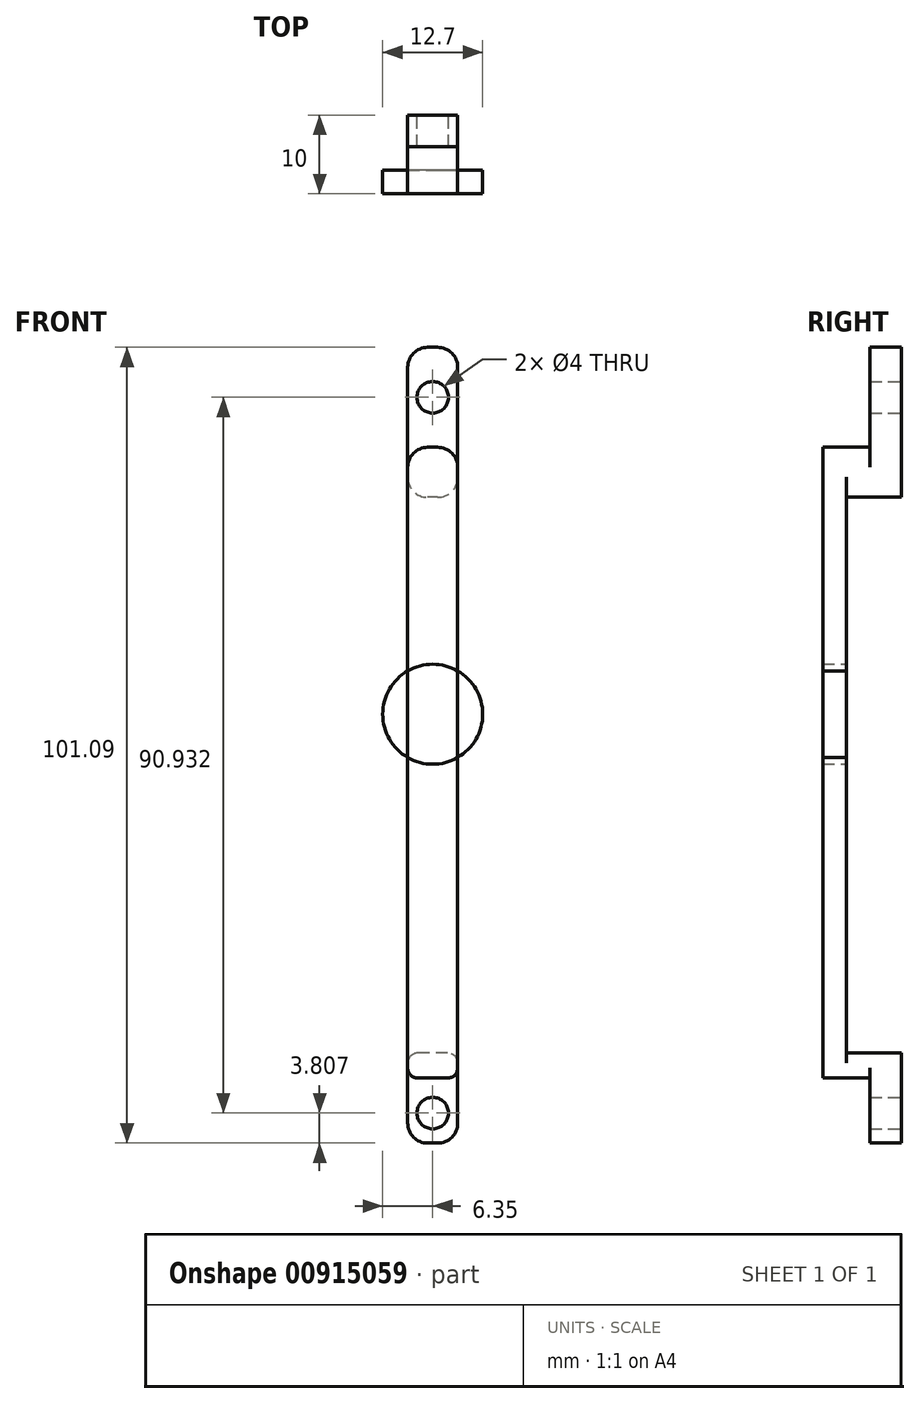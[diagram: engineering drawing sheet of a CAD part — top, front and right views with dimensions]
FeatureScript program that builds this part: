
annotation { "Feature Type Name" : "Feature", "Feature Type Description" : "" }
export const myFeature = defineFeature(function(context is Context, id is Id, definition is map)
    precondition{}
    {
        {
            var Q0;
            Q0=qCreatedBy(makeId("Front.planeOp"),FACE);
            var sketch = newSketch(context, id + "F0", { "sketchPlane" : qUnion([Q0])});
            skCircle(sketch, "E0", {"center": v(0, 0) * mm, "radius": 6.35 * mm});
            skLineSegment(sketch, "E1", {"start": v(0, 0) * mm, "end": v(0, 16.95) * mm, "construction": true});
            skLineSegment(sketch, "E2", {"start": v(0, 0) * mm, "end": v(0, -23.11) * mm, "construction": true});
            skLineSegment(sketch, "E3.bottom", {"start": v(-3.17, 0) * mm, "end": v(3.18, 0) * mm});
            skLineSegment(sketch, "E3.top", {"start": v(-3.17, 33.9) * mm, "end": v(3.18, 33.9) * mm});
            skLineSegment(sketch, "E3.left", {"start": v(-3.17, 0) * mm, "end": v(-3.17, 33.9) * mm});
            skLineSegment(sketch, "E3.right", {"start": v(3.18, 0) * mm, "end": v(3.18, 33.9) * mm});
            skPoint(sketch, "E3.middle", {"position": v(0, 16.95) * mm});
            skLineSegment(sketch, "E4.bottom", {"start": v(3.18, 0) * mm, "end": v(-3.17, 0) * mm});
            skLineSegment(sketch, "E4.top", {"start": v(3.18, -46.23) * mm, "end": v(-3.17, -46.23) * mm});
            skLineSegment(sketch, "E4.left", {"start": v(3.18, 0) * mm, "end": v(3.18, -46.23) * mm});
            skLineSegment(sketch, "E4.right", {"start": v(-3.17, 0) * mm, "end": v(-3.17, -46.23) * mm});
            skPoint(sketch, "E4.middle", {"position": v(0, -23.11) * mm});
            skSolve(sketch);
        }
        {
            var Q0;
            {var subQ5=sQuery(id+"F0.wireOp",EDGE,"E3.top");Q0=makeQuery(id+"F0.imprint","IMPRINT",FACE,{"disambiguationData":[TD([[makeQuery(id+"F0.imprint","IMPRINT",EDGE,{"derivedFrom":subQ5}),-1.0]])]});}
            var Q1;
            {var subQ0=sQuery(id+"F0.wireOp",EDGE,"E3.left");var subQ1=sQuery(id+"F0.wireOp",EDGE,"E0");var subQ2=makeQuery(id+"F0.imprint","INTERSECT",VERTEX,{"derivedFrom":[subQ1,subQ0]});Q1=makeQuery(id+"F0.imprint","IMPRINT",FACE,{"disambiguationData":[TD([[makeQuery(id+"F0.imprint","IMPRINT",EDGE,{"disambiguationData":[TD([[subQ2,-1.0]])],"derivedFrom":subQ1}),1.0]])]});}
            var Q2;
            {var subQ5=sQuery(id+"F0.wireOp",EDGE,"E4.bottom");Q2=makeQuery(id+"F0.imprint","IMPRINT",FACE,{"disambiguationData":[TD([[makeQuery(id+"F0.imprint","IMPRINT",EDGE,{"derivedFrom":subQ5}),-1.0]])]});}
            var Q3;
            {var subQ0=sQuery(id+"F0.wireOp",EDGE,"E3.right");var subQ1=sQuery(id+"F0.wireOp",EDGE,"E0");var subQ2=makeQuery(id+"F0.imprint","INTERSECT",VERTEX,{"derivedFrom":[subQ1,subQ0]});Q3=makeQuery(id+"F0.imprint","IMPRINT",FACE,{"disambiguationData":[TD([[makeQuery(id+"F0.imprint","IMPRINT",EDGE,{"disambiguationData":[TD([[subQ2,1.0]])],"derivedFrom":subQ1}),1.0]])]});}
            var Q4;
            {var subQ5=sQuery(id+"F0.wireOp",EDGE,"E4.bottom");Q4=makeQuery(id+"F0.imprint","IMPRINT",FACE,{"disambiguationData":[TD([[makeQuery(id+"F0.imprint","IMPRINT",EDGE,{"derivedFrom":subQ5}),1.0]])]});}
            var Q5;
            {var subQ5=sQuery(id+"F0.wireOp",EDGE,"E4.top");Q5=makeQuery(id+"F0.imprint","IMPRINT",FACE,{"disambiguationData":[TD([[makeQuery(id+"F0.imprint","IMPRINT",EDGE,{"derivedFrom":subQ5}),-1.0]])]});}
            extrude(context, id + "F1", {"entities" : qUnion([Q0, Q1, Q2, Q3, Q4, Q5]), "depth" : 3 * mm, "offsetDistance" : 25.4 * mm});
        }
        {
            var Q0;
            Q0=makeQuery(id+"F1.opExtrude","CAP_FACE",FACE,{"disambiguationData":[OSD([sQuery(id+"F0.wireOp",EDGE,"E0"),sQuery(id+"F0.wireOp",EDGE,"E3.top"),sQuery(id+"F0.wireOp",EDGE,"E3.left"),sQuery(id+"F0.wireOp",EDGE,"E3.right"),sQuery(id+"F0.wireOp",EDGE,"E4.top"),sQuery(id+"F0.wireOp",EDGE,"E4.left"),sQuery(id+"F0.wireOp",EDGE,"E4.right")])],"isStart":true});
            var sketch = newSketch(context, id + "F2", { "sketchPlane" : qUnion([Q0])});
            skLineSegment(sketch, "E5.bottom", {"start": v(-3.18, 33.9) * mm, "end": v(3.17, 33.9) * mm});
            skLineSegment(sketch, "E5.top", {"start": v(-3.18, 27.56) * mm, "end": v(3.17, 27.56) * mm});
            skLineSegment(sketch, "E5.left", {"start": v(-3.18, 33.9) * mm, "end": v(-3.18, 27.56) * mm});
            skLineSegment(sketch, "E5.right", {"start": v(3.17, 33.9) * mm, "end": v(3.17, 27.56) * mm});
            skLineSegment(sketch, "E6.bottom", {"start": v(-3.18, -46.23) * mm, "end": v(3.17, -46.23) * mm});
            skLineSegment(sketch, "E6.top", {"start": v(-3.18, -43.05) * mm, "end": v(3.17, -43.05) * mm});
            skLineSegment(sketch, "E6.left", {"start": v(-3.18, -46.23) * mm, "end": v(-3.18, -43.05) * mm});
            skLineSegment(sketch, "E6.right", {"start": v(3.17, -46.23) * mm, "end": v(3.17, -43.05) * mm});
            skSolve(sketch);
        }
        {
            var Q0;
            Q0=makeQuery(id+"F2.imprint","IMPRINT",FACE,{"disambiguationData":[TD([[makeQuery(id+"F2.imprint","IMPRINT",EDGE,{"derivedFrom":sQuery(id+"F2.wireOp",EDGE,"E5.bottom")}),1.0]])]});
            var Q1;
            Q1=makeQuery(id+"F2.imprint","IMPRINT",FACE,{"disambiguationData":[TD([[makeQuery(id+"F2.imprint","IMPRINT",EDGE,{"derivedFrom":sQuery(id+"F2.wireOp",EDGE,"E6.bottom")}),1.0]])]});
            extrude(context, id + "F3", {"entities" : qUnion([Q0, Q1]), "operationType" : NewBodyOperationType.ADD, "depth" : 7 * mm, "offsetDistance" : 25.4 * mm});
        }
        {
            var Q0;
            Q0=makeQuery(id+"F3.boolean.opBoolean","MERGE",FACE,{"derivedFrom":[makeQuery(id+"F1.opExtrude","SWEPT_FACE",FACE,{"disambiguationData":[OSD([sQuery(id+"F0.wireOp",EDGE,"E3.top")])]}),makeQuery(id+"F3.opExtrude","SWEPT_FACE",FACE,{"disambiguationData":[OSD([sQuery(id+"F2.wireOp",EDGE,"E5.bottom")])]})]});
            var sketch = newSketch(context, id + "F4", { "sketchPlane" : qUnion([Q0])});
            skLineSegment(sketch, "E7.bottom", {"start": v(3.18, 7) * mm, "end": v(-3.17, 7) * mm});
            skLineSegment(sketch, "E7.top", {"start": v(3.18, 3) * mm, "end": v(-3.17, 3) * mm});
            skLineSegment(sketch, "E7.left", {"start": v(3.18, 7) * mm, "end": v(3.18, 3) * mm});
            skLineSegment(sketch, "E7.right", {"start": v(-3.17, 7) * mm, "end": v(-3.17, 3) * mm});
            skSolve(sketch);
        }
        {
            var Q0;
            Q0=makeQuery(id+"F4.imprint","IMPRINT",FACE,{"disambiguationData":[TD([[makeQuery(id+"F4.imprint","IMPRINT",EDGE,{"derivedFrom":sQuery(id+"F4.wireOp",EDGE,"E7.bottom")}),-1.0]])]});
            extrude(context, id + "F5", {"entities" : qUnion([Q0]), "operationType" : NewBodyOperationType.ADD, "depth" : 12.7 * mm, "offsetDistance" : 25.4 * mm});
        }
        {
            var Q0;
            Q0=makeQuery(id+"F5.boolean.opBoolean","MERGE",FACE,{"derivedFrom":[makeQuery(id+"F3.opExtrude","CAP_FACE",FACE,{"disambiguationData":[OSD([sQuery(id+"F2.wireOp",EDGE,"E5.bottom"),sQuery(id+"F2.wireOp",EDGE,"E5.top"),sQuery(id+"F2.wireOp",EDGE,"E5.left"),sQuery(id+"F2.wireOp",EDGE,"E5.right")])],"isStart":false}),makeQuery(id+"F5.opExtrude","SWEPT_FACE",FACE,{"disambiguationData":[OSD([sQuery(id+"F4.wireOp",EDGE,"E7.bottom")])]})]});
            var sketch = newSketch(context, id + "F6", { "sketchPlane" : qUnion([Q0])});
            skLineSegment(sketch, "E8", {"start": v(0, 46.6) * mm, "end": v(0, 40.26) * mm, "construction": true});
            skCircle(sketch, "E9", {"center": v(0, 40.26) * mm, "radius": 2 * mm});
            skSolve(sketch);
        }
        {
            var Q0;
            Q0=makeQuery(id+"F6.imprint","IMPRINT",FACE,{"disambiguationData":[TD([[makeQuery(id+"F6.imprint","IMPRINT",EDGE,{"derivedFrom":sQuery(id+"F6.wireOp",EDGE,"E9")}),1.0]])]});
            extrude(context, id + "F7", {"entities" : qUnion([Q0]), "operationType" : NewBodyOperationType.REMOVE, "oppositeDirection" : true, "depth" : 25.4 * mm, "offsetDistance" : 25.4 * mm});
        }
        {
            var Q0;
            Q0=makeQuery(id+"F3.boolean.opBoolean","MERGE",FACE,{"derivedFrom":[makeQuery(id+"F1.opExtrude","SWEPT_FACE",FACE,{"disambiguationData":[OSD([sQuery(id+"F0.wireOp",EDGE,"E4.top")])]}),makeQuery(id+"F3.opExtrude","SWEPT_FACE",FACE,{"disambiguationData":[OSD([sQuery(id+"F2.wireOp",EDGE,"E6.bottom")])]})]});
            var sketch = newSketch(context, id + "F8", { "sketchPlane" : qUnion([Q0])});
            skLineSegment(sketch, "E10.bottom", {"start": v(-3.17, -7) * mm, "end": v(3.18, -7) * mm});
            skLineSegment(sketch, "E10.top", {"start": v(-3.17, -3) * mm, "end": v(3.18, -3) * mm});
            skLineSegment(sketch, "E10.left", {"start": v(-3.17, -7) * mm, "end": v(-3.17, -3) * mm});
            skLineSegment(sketch, "E10.right", {"start": v(3.18, -7) * mm, "end": v(3.18, -3) * mm});
            skSolve(sketch);
        }
        {
            var Q0;
            Q0=makeQuery(id+"F8.imprint","IMPRINT",FACE,{"disambiguationData":[TD([[makeQuery(id+"F8.imprint","IMPRINT",EDGE,{"derivedFrom":sQuery(id+"F8.wireOp",EDGE,"E10.bottom")}),-1.0]])]});
            extrude(context, id + "F9", {"entities" : qUnion([Q0]), "operationType" : NewBodyOperationType.ADD, "depth" : 8.25 * mm, "offsetDistance" : 25.4 * mm});
        }
        {
            var Q0;
            Q0=makeQuery(id+"F9.boolean.opBoolean","MERGE",FACE,{"derivedFrom":[makeQuery(id+"F3.opExtrude","CAP_FACE",FACE,{"disambiguationData":[OSD([sQuery(id+"F2.wireOp",EDGE,"E6.bottom"),sQuery(id+"F2.wireOp",EDGE,"E6.top"),sQuery(id+"F2.wireOp",EDGE,"E6.left"),sQuery(id+"F2.wireOp",EDGE,"E6.right")])],"isStart":false}),makeQuery(id+"F9.opExtrude","SWEPT_FACE",FACE,{"disambiguationData":[OSD([sQuery(id+"F8.wireOp",EDGE,"E10.bottom")])]})]});
            var sketch = newSketch(context, id + "F10", { "sketchPlane" : qUnion([Q0])});
            skLineSegment(sketch, "E11", {"start": v(0, -54.48) * mm, "end": v(0, -50.67) * mm, "construction": true});
            skCircle(sketch, "E12", {"center": v(0, -50.67) * mm, "radius": 2 * mm});
            skSolve(sketch);
        }
        {
            var Q0;
            Q0=makeQuery(id+"F10.imprint","IMPRINT",FACE,{"disambiguationData":[TD([[makeQuery(id+"F10.imprint","IMPRINT",EDGE,{"derivedFrom":sQuery(id+"F10.wireOp",EDGE,"E12")}),1.0]])]});
            extrude(context, id + "F11", {"entities" : qUnion([Q0]), "operationType" : NewBodyOperationType.REMOVE, "oppositeDirection" : true, "depth" : 25.4 * mm, "offsetDistance" : 25.4 * mm});
        }
        {
            var Q0;
            Q0=makeQuery(id+"F5.opExtrude","CAP_EDGE",EDGE,{"disambiguationData":[OSD([sQuery(id+"F4.wireOp",EDGE,"E7.right")])],"isStart":false});
            var Q1;
            Q1=makeQuery(id+"F5.opExtrude","CAP_EDGE",EDGE,{"disambiguationData":[OSD([sQuery(id+"F4.wireOp",EDGE,"E7.left")])],"isStart":false});
            var Q2;
            Q2=makeQuery(id+"F3.opExtrude","SWEPT_EDGE",EDGE,{"disambiguationData":[OSD([sQuery(id+"F0.wireOp",EDGE,"E3.left"),sQuery(id+"F2.wireOp",EDGE,"E5.top"),sQuery(id+"F2.wireOp",EDGE,"E5.right")])]});
            var Q3;
            Q3=makeQuery(id+"F3.boolean.opBoolean","MERGE",EDGE,{"derivedFrom":[makeQuery(id+"F1.opExtrude","SWEPT_EDGE",EDGE,{"disambiguationData":[OSD([sQuery(id+"F0.wireOp",EDGE,"E3.top"),sQuery(id+"F0.wireOp",EDGE,"E3.right")])]}),makeQuery(id+"F3.opExtrude","SWEPT_EDGE",EDGE,{"disambiguationData":[OSD([sQuery(id+"F2.wireOp",EDGE,"E5.bottom"),sQuery(id+"F2.wireOp",EDGE,"E5.left")])]})]});
            var Q4;
            Q4=makeQuery(id+"F3.boolean.opBoolean","MERGE",EDGE,{"derivedFrom":[makeQuery(id+"F1.opExtrude","SWEPT_EDGE",EDGE,{"disambiguationData":[OSD([sQuery(id+"F0.wireOp",EDGE,"E3.top"),sQuery(id+"F0.wireOp",EDGE,"E3.left")])]}),makeQuery(id+"F3.opExtrude","SWEPT_EDGE",EDGE,{"disambiguationData":[OSD([sQuery(id+"F2.wireOp",EDGE,"E5.bottom"),sQuery(id+"F2.wireOp",EDGE,"E5.right")])]})]});
            var Q5;
            Q5=makeQuery(id+"F3.opExtrude","SWEPT_EDGE",EDGE,{"disambiguationData":[OSD([sQuery(id+"F0.wireOp",EDGE,"E3.right"),sQuery(id+"F2.wireOp",EDGE,"E5.top"),sQuery(id+"F2.wireOp",EDGE,"E5.left")])]});
            var Q6;
            Q6=makeQuery(id+"F9.opExtrude","CAP_EDGE",EDGE,{"disambiguationData":[OSD([sQuery(id+"F8.wireOp",EDGE,"E10.left")])],"isStart":false});
            var Q7;
            Q7=makeQuery(id+"F9.opExtrude","CAP_EDGE",EDGE,{"disambiguationData":[OSD([sQuery(id+"F8.wireOp",EDGE,"E10.right")])],"isStart":false});
            fillet(context, id + "F12", {"entities" : qUnion([Q0, Q1, Q2, Q3, Q4, Q5, Q6, Q7]), "radius" : 2.54 * mm, "tangentPropagation" : true, "allowEdgeOverflow" : false});
        }
        {
            var Q0;
            Q0=makeQuery(id+"F3.opExtrude","SWEPT_EDGE",EDGE,{"disambiguationData":[OSD([sQuery(id+"F0.wireOp",EDGE,"E4.left"),sQuery(id+"F2.wireOp",EDGE,"E6.top"),sQuery(id+"F2.wireOp",EDGE,"E6.left")])]});
            var Q1;
            Q1=makeQuery(id+"F3.opExtrude","SWEPT_EDGE",EDGE,{"disambiguationData":[OSD([sQuery(id+"F0.wireOp",EDGE,"E4.right"),sQuery(id+"F2.wireOp",EDGE,"E6.top"),sQuery(id+"F2.wireOp",EDGE,"E6.right")])]});
            var Q2;
            Q2=makeQuery(id+"F3.boolean.opBoolean","MERGE",EDGE,{"derivedFrom":[makeQuery(id+"F1.opExtrude","SWEPT_EDGE",EDGE,{"disambiguationData":[OSD([sQuery(id+"F0.wireOp",EDGE,"E4.top"),sQuery(id+"F0.wireOp",EDGE,"E4.left")])]}),makeQuery(id+"F3.opExtrude","SWEPT_EDGE",EDGE,{"disambiguationData":[OSD([sQuery(id+"F2.wireOp",EDGE,"E6.bottom"),sQuery(id+"F2.wireOp",EDGE,"E6.left")])]})]});
            var Q3;
            Q3=makeQuery(id+"F3.boolean.opBoolean","MERGE",EDGE,{"derivedFrom":[makeQuery(id+"F1.opExtrude","SWEPT_EDGE",EDGE,{"disambiguationData":[OSD([sQuery(id+"F0.wireOp",EDGE,"E4.top"),sQuery(id+"F0.wireOp",EDGE,"E4.right")])]}),makeQuery(id+"F3.opExtrude","SWEPT_EDGE",EDGE,{"disambiguationData":[OSD([sQuery(id+"F2.wireOp",EDGE,"E6.bottom"),sQuery(id+"F2.wireOp",EDGE,"E6.right")])]})]});
            fillet(context, id + "F13", {"entities" : qUnion([Q0, Q1, Q2, Q3]), "radius" : 1.27 * mm, "tangentPropagation" : true, "allowEdgeOverflow" : false});
        }
    });
